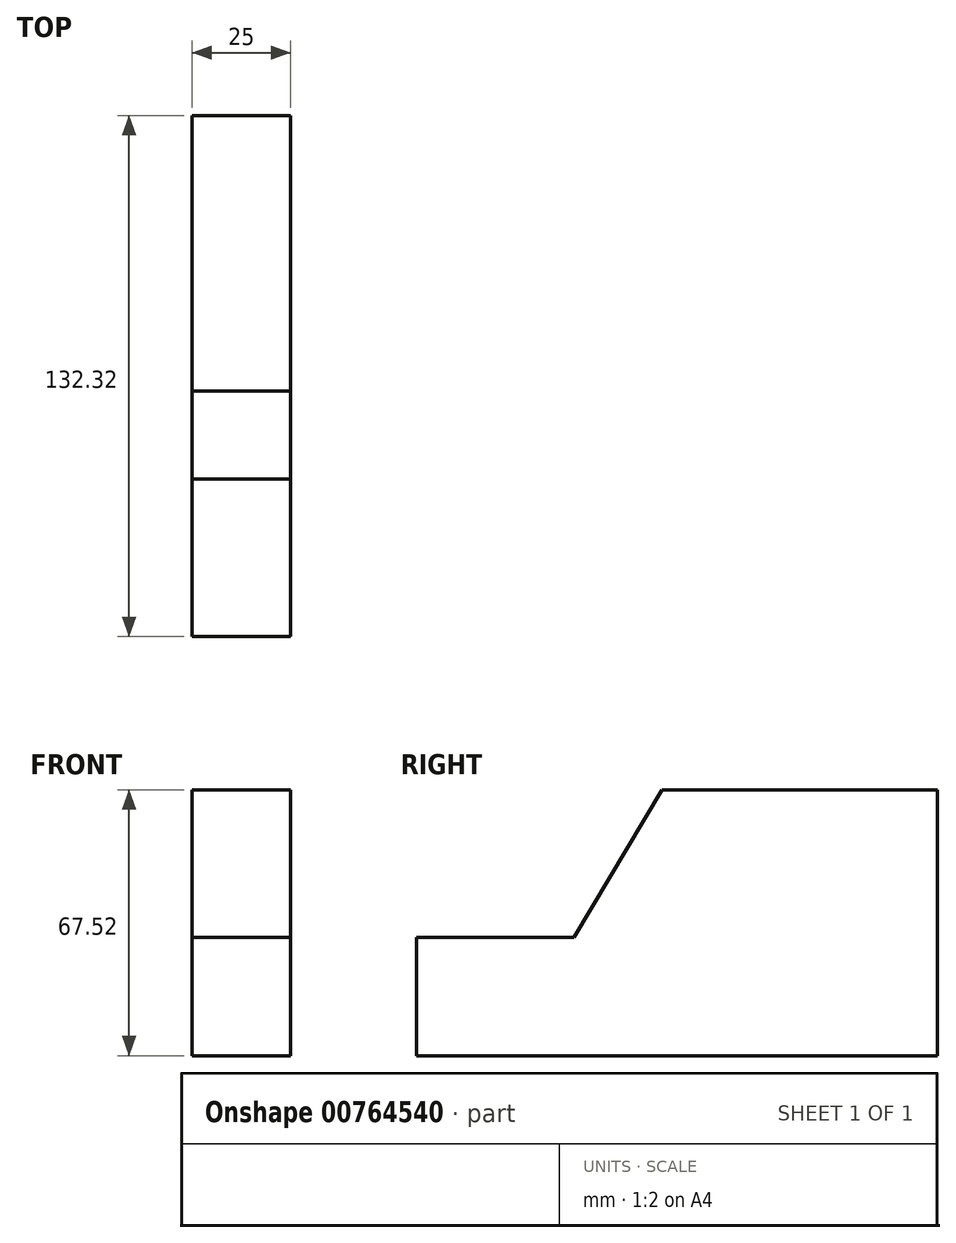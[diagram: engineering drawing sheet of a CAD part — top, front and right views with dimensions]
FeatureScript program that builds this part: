
annotation { "Feature Type Name" : "Feature", "Feature Type Description" : "" }
export const myFeature = defineFeature(function(context is Context, id is Id, definition is map)
    precondition{}
    {
        {
            var Q0;
            Q0=qCreatedBy(makeId("Right.planeOp"),FACE);
            var sketch = newSketch(context, id + "F0", { "sketchPlane" : qUnion([Q0])});
            skLineSegment(sketch, "E0", {"start": v(-62.52, 0) * mm, "end": v(57.48, 0) * mm});
            skLineSegment(sketch, "E1", {"start": v(-62.52, 0) * mm, "end": v(-62.52, 30) * mm});
            skLineSegment(sketch, "E2", {"start": v(-62.52, 30) * mm, "end": v(-22.52, 30) * mm});
            skLineSegment(sketch, "E3", {"start": v(-22.52, 30) * mm, "end": v(-0.2, 67.52) * mm});
            skLineSegment(sketch, "E4", {"start": v(-0.2, 67.52) * mm, "end": v(69.8, 67.52) * mm});
            skLineSegment(sketch, "E5", {"start": v(69.8, 67.52) * mm, "end": v(69.8, 0) * mm});
            skLineSegment(sketch, "E6", {"start": v(57.48, 0) * mm, "end": v(69.8, 0) * mm});
            skSolve(sketch);
        }
        {
            var Q0;
            Q0 = qSketchRegion(id + "F0", true);
            extrude(context, id + "F1", {"entities" : qUnion([Q0]), "depth" : 25 * mm, "offsetDistance" : 25 * mm});
        }
    });
